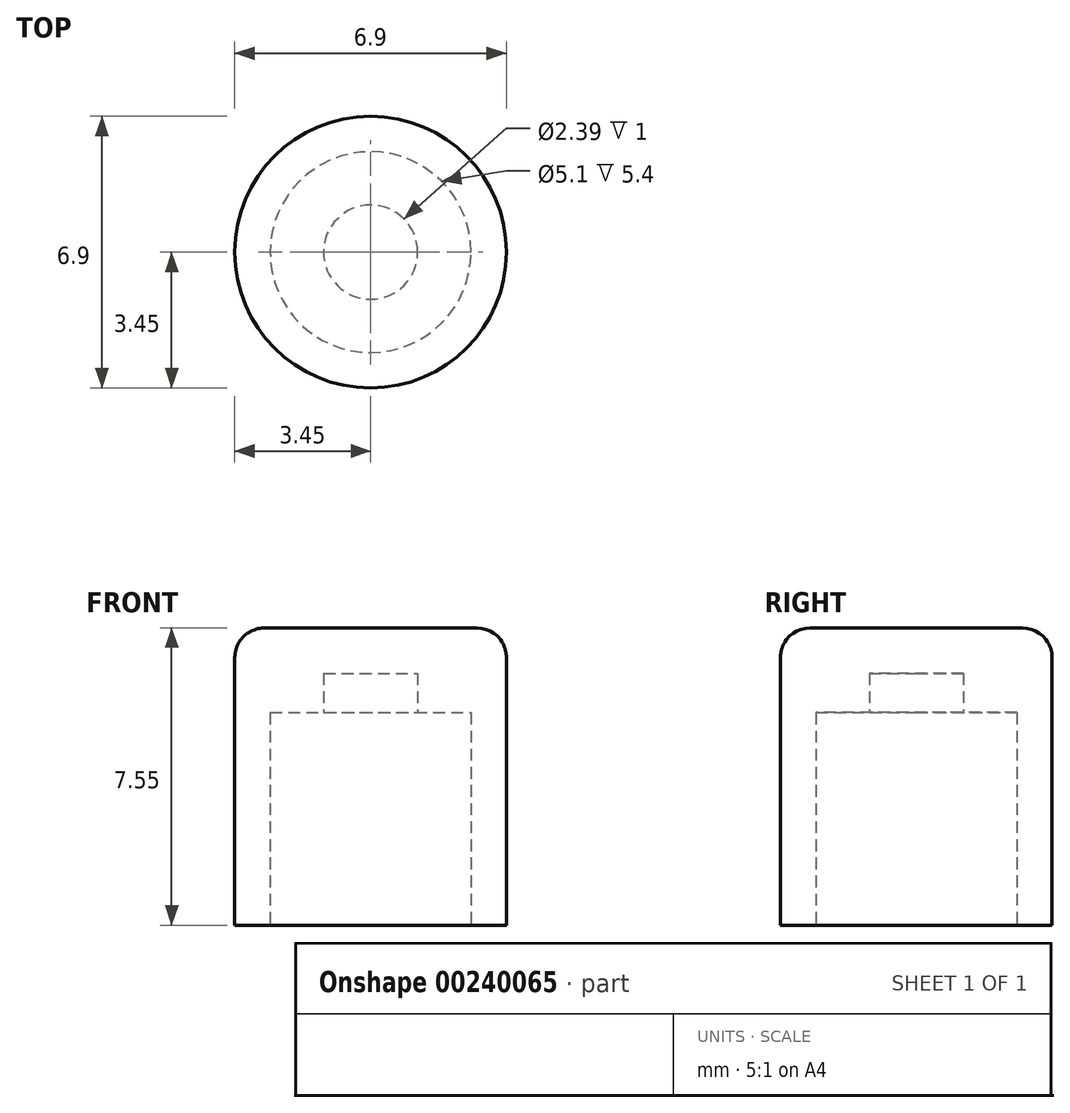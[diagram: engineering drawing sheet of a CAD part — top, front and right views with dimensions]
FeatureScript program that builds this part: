
annotation { "Feature Type Name" : "Feature", "Feature Type Description" : "" }
export const myFeature = defineFeature(function(context is Context, id is Id, definition is map)
    precondition{}
    {
        {
            var Q0;
            Q0=qCreatedBy(makeId("Front.planeOp"),FACE);
            var sketch = newSketch(context, id + "F0", { "sketchPlane" : qUnion([Q0])});
            skLineSegment(sketch, "E0", {"start": v(0, 0) * mm, "end": v(0, 56.55) * mm, "construction": true});
            skSolve(sketch);
        }
        {
            var Q0;
            Q0=qCreatedBy(makeId("Front.planeOp"),FACE);
            var sketch = newSketch(context, id + "F1", { "sketchPlane" : qUnion([Q0])});
            skLineSegment(sketch, "E1", {"start": v(2.55, 0) * mm, "end": v(2.55, 5.4) * mm});
            skLineSegment(sketch, "E2", {"start": v(2.55, 5.4) * mm, "end": v(1.2, 5.4) * mm});
            skLineSegment(sketch, "E3", {"start": v(1.2, 5.4) * mm, "end": v(1.2, 6.4) * mm});
            skLineSegment(sketch, "E4", {"start": v(1.2, 6.4) * mm, "end": v(0, 6.4) * mm});
            skLineSegment(sketch, "E5", {"start": v(0, 6.4) * mm, "end": v(0, 7.55) * mm});
            skLineSegment(sketch, "E6", {"start": v(0, 7.55) * mm, "end": v(2.7, 7.55) * mm});
            skLineSegment(sketch, "E7", {"start": v(3.45, 6.8) * mm, "end": v(3.45, 0) * mm});
            skLineSegment(sketch, "E8", {"start": v(3.45, 0) * mm, "end": v(2.55, 0) * mm});
            skPoint(sketch, "E9.visualSharp", {"position": v(3.45, 7.55) * mm});
            skArc(sketch, "E9.filletArc", {"start": v(3.45, 6.8) * mm, "mid": v(3.23, 7.33) * mm, "end": v(2.7, 7.55) * mm});
            skSolve(sketch);
        }
        {
            var Q0;
            Q0 = qSketchRegion(id + "F1", true);
            var Q1;
            Q1=sQuery(id+"F0.wireOp",EDGE,"E0");
            revolve(context, id + "F2", {"entities" : qUnion([Q0]), "axis" : qUnion([Q1]), "revolveType" : RevolveType.FULL});
        }
    });
